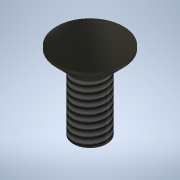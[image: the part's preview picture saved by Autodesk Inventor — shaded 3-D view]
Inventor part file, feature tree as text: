
AUTODESK INVENTOR PART (.ipt)
format: ipt  version: 2020.2 (Build 242310000, 310)  size: 128,000 bytes
history: native  units: mm
features: extrude x3, sketch x3, other x1, thread x1, chamfer x1
ambient origin geometry x1: Origin
bodies: Body1 (feature_tree)
feature tree (9):
  other  "ソリッド1"
  extrude  "押し出し1"  Depth=2.6mm
  extrude  "押し出し2"  Depth=6.0mm TaperAngle=0.0deg
  thread  "ねじ1"
  chamfer  "面取り1"  Distance=5.2mm
  extrude  "押し出し4"  Depth=1.5mm TaperAngle=0.0deg
  sketch  "スケッチ1"
  sketch  "スケッチ2"
  sketch  "スケッチ4"
